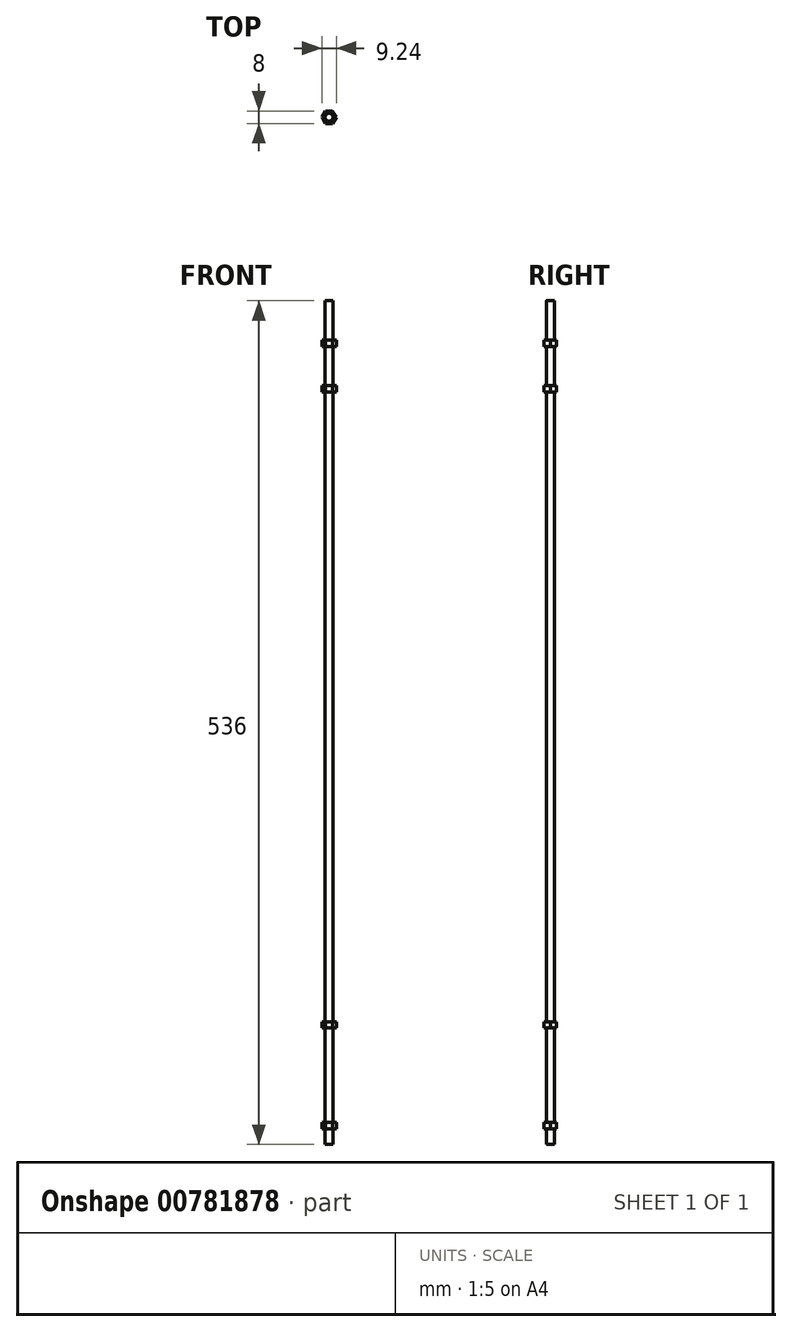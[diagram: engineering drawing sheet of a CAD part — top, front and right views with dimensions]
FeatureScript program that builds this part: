
annotation { "Feature Type Name" : "Feature", "Feature Type Description" : "" }
export const myFeature = defineFeature(function(context is Context, id is Id, definition is map)
    precondition{}
    {
        {
            var Q0;
            Q0=qCreatedBy(makeId("Top.planeOp"),FACE);
            var sketch = newSketch(context, id + "F0", { "sketchPlane" : qUnion([Q0])});
            skCircle(sketch, "E0", {"center": v(0, 0) * mm, "radius": 2.5 * mm});
            skSolve(sketch);
        }
        {
            var Q0;
            Q0=qSketchRegion(id+"F0",true);
            extrude(context, id + "F1", {"entities" : qUnion([Q0]), "depth" : 400 * mm});
        }
        {
            var Q0;
            Q0=makeQuery(id+"F1.opExtrude","CAP_FACE",FACE,{"disambiguationData":[OSD([sQuery(id+"F0.wireOp",EDGE,"E0")])],"isStart":true});
            var sketch = newSketch(context, id + "F2", { "sketchPlane" : qUnion([Q0])});
            skCircle(sketch, "E1.cCircle", {"center": v(0, 0) * mm, "radius": 4 * mm, "construction": true});
            skLineSegment(sketch, "E1.0", {"start": v(-2.3, 4) * mm, "end": v(2.3, 4) * mm});
            skLineSegment(sketch, "E1.1", {"start": v(2.3, 4) * mm, "end": v(4.62, 0) * mm});
            skLineSegment(sketch, "E1.2", {"start": v(4.62, 0) * mm, "end": v(2.3, -4) * mm});
            skLineSegment(sketch, "E1.3", {"start": v(2.3, -4) * mm, "end": v(-2.3, -4) * mm});
            skLineSegment(sketch, "E1.4", {"start": v(-2.3, -4) * mm, "end": v(-4.62, 0) * mm});
            skLineSegment(sketch, "E1.5", {"start": v(-4.62, 0) * mm, "end": v(-2.3, 4) * mm});
            skPoint(sketch, "E1.0.midPoint", {"position": v(0, 4) * mm});
            skSolve(sketch);
        }
        {
            var Q0;
            Q0=qSketchRegion(id+"F2",true);
            extrude(context, id + "F3", {"entities" : qUnion([Q0]), "operationType" : NewBodyOperationType.ADD, "depth" : 4 * mm});
        }
        {
            var Q0;
            Q0=makeQuery(id+"F3.opExtrude","CAP_FACE",FACE,{"disambiguationData":[OSD([sQuery(id+"F2.wireOp",EDGE,"E1.0"),sQuery(id+"F2.wireOp",EDGE,"E1.1"),sQuery(id+"F2.wireOp",EDGE,"E1.2"),sQuery(id+"F2.wireOp",EDGE,"E1.3"),sQuery(id+"F2.wireOp",EDGE,"E1.4"),sQuery(id+"F2.wireOp",EDGE,"E1.5")])],"isStart":false});
            var sketch = newSketch(context, id + "F4", { "sketchPlane" : qUnion([Q0])});
            skCircle(sketch, "E2.0", {"center": v(0, 0) * mm, "radius": 2.5 * mm});
            skSolve(sketch);
        }
        {
            var Q0;
            Q0=qSketchRegion(id+"F4",true);
            extrude(context, id + "F5", {"entities" : qUnion([Q0]), "operationType" : NewBodyOperationType.ADD, "depth" : 60 * mm});
        }
        {
            var Q0;
            Q0=makeQuery(id+"F5.opExtrude","CAP_FACE",FACE,{"disambiguationData":[OSD([sQuery(id+"F4.wireOp",EDGE,"E2.0")])],"isStart":false});
            var sketch = newSketch(context, id + "F6", { "sketchPlane" : qUnion([Q0])});
            skLineSegment(sketch, "E3.0.0", {"start": v(2.3, 4) * mm, "end": v(-2.3, 4) * mm});
            skLineSegment(sketch, "E3.0.1", {"start": v(-2.3, 4) * mm, "end": v(-4.62, 0) * mm});
            skLineSegment(sketch, "E3.0.2", {"start": v(-4.62, 0) * mm, "end": v(-2.3, -4) * mm});
            skLineSegment(sketch, "E3.0.3", {"start": v(-2.3, -4) * mm, "end": v(2.3, -4) * mm});
            skLineSegment(sketch, "E3.0.4", {"start": v(2.3, -4) * mm, "end": v(4.62, 0) * mm});
            skLineSegment(sketch, "E3.0.5", {"start": v(4.62, 0) * mm, "end": v(2.3, 4) * mm});
            skSolve(sketch);
        }
        {
            var Q0;
            Q0=qSketchRegion(id+"F6",true);
            extrude(context, id + "F7", {"entities" : qUnion([Q0]), "operationType" : NewBodyOperationType.ADD, "depth" : 4 * mm});
        }
        {
            var Q0;
            Q0=makeQuery(id+"F1.opExtrude","CAP_FACE",FACE,{"disambiguationData":[OSD([sQuery(id+"F0.wireOp",EDGE,"E0")])],"isStart":false});
            var sketch = newSketch(context, id + "F8", { "sketchPlane" : qUnion([Q0])});
            skLineSegment(sketch, "E4.0.0", {"start": v(-2.3, -4) * mm, "end": v(2.3, -4) * mm});
            skLineSegment(sketch, "E4.0.1", {"start": v(2.3, -4) * mm, "end": v(4.62, 0) * mm});
            skLineSegment(sketch, "E4.0.2", {"start": v(4.62, 0) * mm, "end": v(2.3, 4) * mm});
            skLineSegment(sketch, "E4.0.3", {"start": v(2.3, 4) * mm, "end": v(-2.3, 4) * mm});
            skLineSegment(sketch, "E4.0.4", {"start": v(-2.3, 4) * mm, "end": v(-4.62, 0) * mm});
            skLineSegment(sketch, "E4.0.5", {"start": v(-4.62, 0) * mm, "end": v(-2.3, -4) * mm});
            skSolve(sketch);
        }
        {
            var Q0;
            Q0=qSketchRegion(id+"F8",true);
            extrude(context, id + "F9", {"entities" : qUnion([Q0]), "operationType" : NewBodyOperationType.ADD, "depth" : 4 * mm});
        }
        {
            var Q0;
            Q0=makeQuery(id+"F9.opExtrude","CAP_FACE",FACE,{"disambiguationData":[OSD([sQuery(id+"F8.wireOp",EDGE,"E4.0.0"),sQuery(id+"F8.wireOp",EDGE,"E4.0.1"),sQuery(id+"F8.wireOp",EDGE,"E4.0.2"),sQuery(id+"F8.wireOp",EDGE,"E4.0.3"),sQuery(id+"F8.wireOp",EDGE,"E4.0.4"),sQuery(id+"F8.wireOp",EDGE,"E4.0.5")])],"isStart":false});
            var sketch = newSketch(context, id + "F10", { "sketchPlane" : qUnion([Q0])});
            skCircle(sketch, "E5.0", {"center": v(0, 0) * mm, "radius": 2.5 * mm});
            skSolve(sketch);
        }
        {
            var Q0;
            Q0=qSketchRegion(id+"F10",true);
            extrude(context, id + "F11", {"entities" : qUnion([Q0]), "operationType" : NewBodyOperationType.ADD, "depth" : 25 * mm});
        }
        {
            var Q0;
            Q0=makeQuery(id+"F11.opExtrude","CAP_FACE",FACE,{"disambiguationData":[OSD([sQuery(id+"F10.wireOp",EDGE,"E5.0")])],"isStart":false});
            var sketch = newSketch(context, id + "F12", { "sketchPlane" : qUnion([Q0])});
            skLineSegment(sketch, "E6.0.0", {"start": v(-4.62, 0) * mm, "end": v(-2.3, -4) * mm});
            skLineSegment(sketch, "E6.0.1", {"start": v(-2.3, -4) * mm, "end": v(2.3, -4) * mm});
            skLineSegment(sketch, "E6.0.2", {"start": v(2.3, -4) * mm, "end": v(4.62, 0) * mm});
            skLineSegment(sketch, "E6.0.3", {"start": v(4.62, 0) * mm, "end": v(2.3, 4) * mm});
            skLineSegment(sketch, "E6.0.4", {"start": v(2.3, 4) * mm, "end": v(-2.3, 4) * mm});
            skLineSegment(sketch, "E6.0.5", {"start": v(-2.3, 4) * mm, "end": v(-4.62, 0) * mm});
            skSolve(sketch);
        }
        {
            var Q0;
            Q0=qSketchRegion(id+"F12",true);
            extrude(context, id + "F13", {"entities" : qUnion([Q0]), "operationType" : NewBodyOperationType.ADD, "depth" : 4 * mm});
        }
        {
            var Q0;
            Q0=makeQuery(id+"F13.opExtrude","CAP_FACE",FACE,{"disambiguationData":[OSD([sQuery(id+"F12.wireOp",EDGE,"E6.0.0"),sQuery(id+"F12.wireOp",EDGE,"E6.0.1"),sQuery(id+"F12.wireOp",EDGE,"E6.0.2"),sQuery(id+"F12.wireOp",EDGE,"E6.0.3"),sQuery(id+"F12.wireOp",EDGE,"E6.0.4"),sQuery(id+"F12.wireOp",EDGE,"E6.0.5")])],"isStart":false});
            var sketch = newSketch(context, id + "F14", { "sketchPlane" : qUnion([Q0])});
            skCircle(sketch, "E7.0", {"center": v(0, 0) * mm, "radius": 2.5 * mm});
            skSolve(sketch);
        }
        {
            var Q0;
            Q0=qSketchRegion(id+"F14",true);
            extrude(context, id + "F15", {"entities" : qUnion([Q0]), "operationType" : NewBodyOperationType.ADD, "depth" : 25 * mm});
        }
        {
            var Q0;
            Q0=makeQuery(id+"F7.opExtrude","CAP_FACE",FACE,{"disambiguationData":[OSD([sQuery(id+"F6.wireOp",EDGE,"E3.0.0"),sQuery(id+"F6.wireOp",EDGE,"E3.0.1"),sQuery(id+"F6.wireOp",EDGE,"E3.0.2"),sQuery(id+"F6.wireOp",EDGE,"E3.0.3"),sQuery(id+"F6.wireOp",EDGE,"E3.0.4"),sQuery(id+"F6.wireOp",EDGE,"E3.0.5")])],"isStart":false});
            var sketch = newSketch(context, id + "F16", { "sketchPlane" : qUnion([Q0])});
            skCircle(sketch, "E8.0", {"center": v(0, 0) * mm, "radius": 2.5 * mm});
            skSolve(sketch);
        }
        {
            var Q0;
            Q0=qSketchRegion(id+"F16",true);
            extrude(context, id + "F17", {"entities" : qUnion([Q0]), "operationType" : NewBodyOperationType.ADD, "depth" : 10 * mm});
        }
    });
